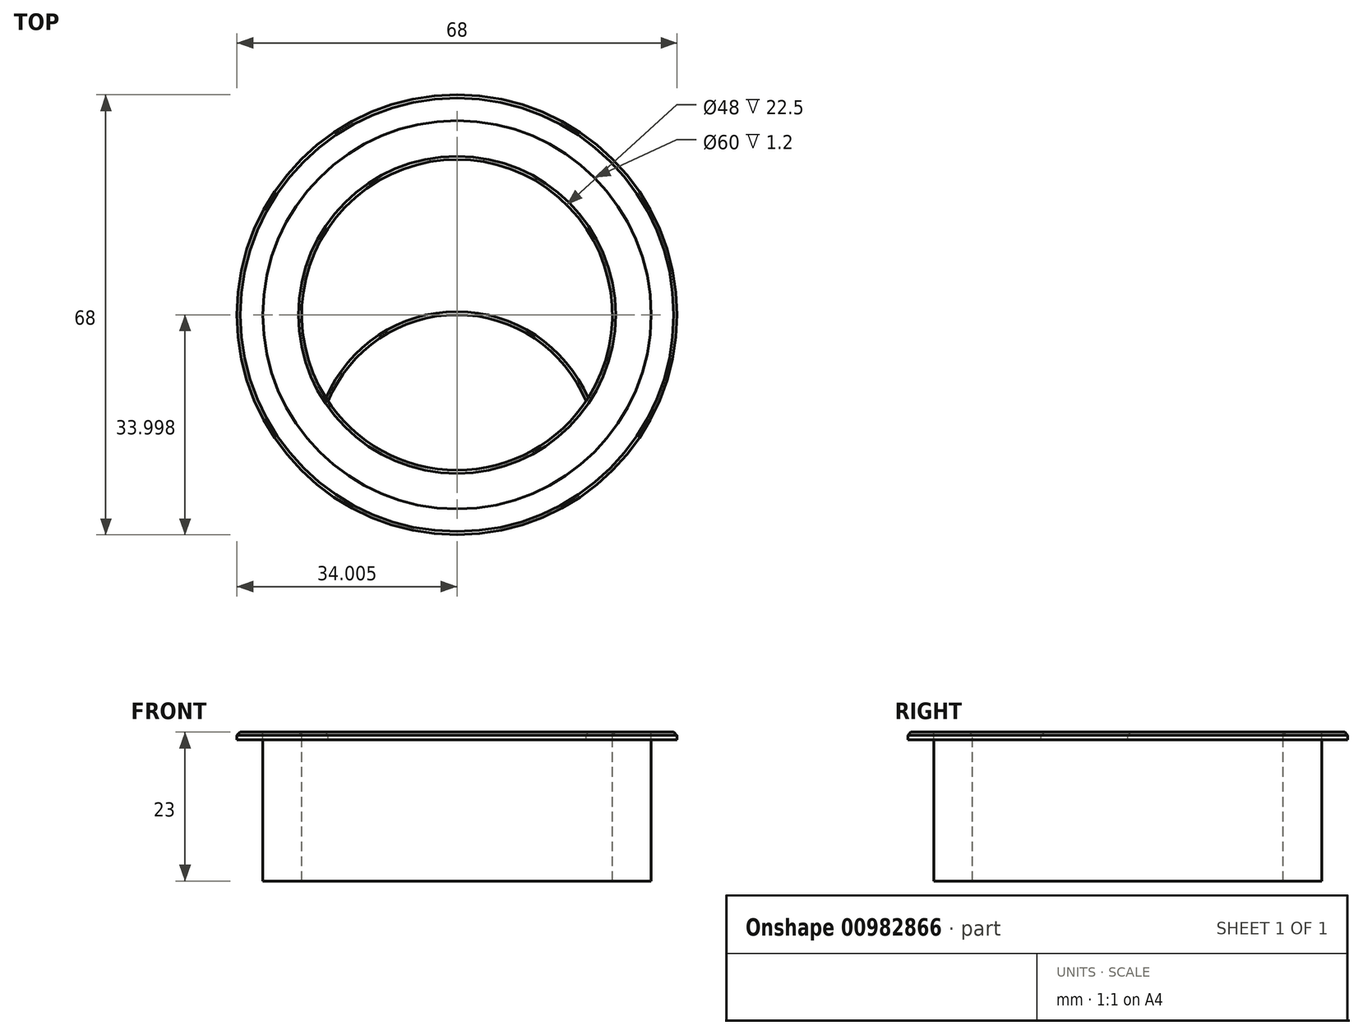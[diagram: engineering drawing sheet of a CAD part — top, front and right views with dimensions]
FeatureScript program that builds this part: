
annotation { "Feature Type Name" : "Feature", "Feature Type Description" : "" }
export const myFeature = defineFeature(function(context is Context, id is Id, definition is map)
    precondition{}
    {
        {
            var Q0;
            Q0=qCreatedBy(makeId("Top.planeOp"),FACE);
            var sketch = newSketch(context, id + "F0", { "sketchPlane" : qUnion([Q0])});
            skCircle(sketch, "E0", {"center": v(-65.17, 13.38) * mm, "radius": 30 * mm});
            skCircle(sketch, "E1", {"center": v(-65.17, 13.38) * mm, "radius": 34 * mm});
            skCircle(sketch, "E2", {"center": v(-65.17, 13.38) * mm, "radius": 24 * mm});
            skArc(sketch, "E3", {"start": v(-45.24, 0) * mm, "mid": v(-65.17, 13.38) * mm, "end": v(-85.1, 0) * mm});
            skSolve(sketch);
        }
        {
            var Q0;
            Q0=makeQuery(id+"F0.imprint","IMPRINT",FACE,{"disambiguationData":[TD([[makeQuery(id+"F0.imprint","IMPRINT",EDGE,{"derivedFrom":sQuery(id+"F0.wireOp",EDGE,"E0")}),-1.0]])]});
            var Q1;
            {var subQ0=sQuery(id+"F0.wireOp",EDGE,"E3");Q1=makeQuery(id+"F0.imprint","IMPRINT",FACE,{"disambiguationData":[TD([[makeQuery(id+"F0.imprint","IMPRINT",EDGE,{"derivedFrom":subQ0}),-1.0]])]});}
            extrude(context, id + "F1", {"entities" : qUnion([Q0, Q1]), "oppositeDirection" : true, "depth" : 1.2 * mm, "offsetDistance" : 25 * mm});
        }
        {
            var Q0;
            Q0=makeQuery(id+"F0.imprint","IMPRINT",FACE,{"disambiguationData":[TD([[makeQuery(id+"F0.imprint","IMPRINT",EDGE,{"derivedFrom":sQuery(id+"F0.wireOp",EDGE,"E0")}),1.0]])]});
            extrude(context, id + "F2", {"entities" : qUnion([Q0]), "oppositeDirection" : true, "depth" : 23 * mm, "offsetDistance" : 25 * mm});
        }
        {
            var Q0;
            Q0=makeQuery(id+"F1.opExtrude","CAP_EDGE",EDGE,{"disambiguationData":[OSD([sQuery(id+"F0.wireOp",EDGE,"E1")])],"isStart":true});
            var Q1;
            Q1=makeQuery(id+"F1.opExtrude","CAP_EDGE",EDGE,{"disambiguationData":[OSD([sQuery(id+"F0.wireOp",EDGE,"E3")])],"isStart":true});
            var Q2;
            Q2=makeQuery(id+"F2.opExtrude","CAP_EDGE",EDGE,{"disambiguationData":[OSD([sQuery(id+"F0.wireOp",EDGE,"E2")])],"isStart":true});
            chamfer(context, id + "F3", {"entities" : qUnion([Q0, Q1, Q2]), "width" : 0.5 * mm, "tangentPropagation" : true});
        }
    });
